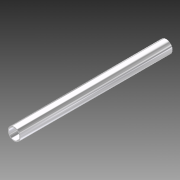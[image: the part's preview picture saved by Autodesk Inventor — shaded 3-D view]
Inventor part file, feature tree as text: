
AUTODESK INVENTOR PART (.ipt)
format: ipt  version: 2011 (Build 150239000, 239)  size: 72,704 bytes
history: native  units: in
note: dims shown in document units (in); Inventor stores cm internally (conversion verified against a paired STEP export)
features: extrude x1, sketch x1
ambient origin geometry x8: Origin, YZ Plane, XZ Plane, XY Plane, X Axis, Y Axis, Z Axis, Center Point
bodies: Solid1 (feature_tree)
feature tree (2):
  extrude  "Extrusion1"  Depth=0.95in
  sketch  "Sketch1"  dims[d0=1.125in d1=0.95in d2=13.5in d3=0.0in]
